FCSTD DOCUMENT  (FreeCAD 0.21R33694 (Git))
Label: archimedes_parametric
License: All rights reserved
LicenseURL: http://en.wikipedia.org/wiki/All_rights_reserved
objects: Part::Part2DObjectPython×3, Part::FeaturePython×3, Sketcher::SketchObject×1, Spreadsheet::Sheet×1
note: 7 computed .brp shape members not serialized (recipe doc carries the construction recipe); baked Part::Feature solids carry a one-line shape summary decoded from their .brp

FEATURE [Sketcher::SketchObject] Sketch
  FullyConstrained = false
  expr: Constraints[51] = <<d>>.diameter
  sketch-geometry (17):
    g0: LineSegment StartX=-33.681 StartY=498.864 StartZ=0 EndX=-186.392 EndY=463.959 EndZ=0
    g1: LineSegment StartX=-209.626 StartY=453.935 StartZ=0 EndX=-339.799 EndY=366.792 EndZ=0
    g2: LineSegment StartX=-347.473 StartY=359.531 StartZ=0 EndX=-441.67 EndY=234.366 EndZ=0
    g3: LineSegment StartX=-462.362 StartY=190.318 StartZ=0 EndX=-498.561 EndY=37.9083 EndZ=0
    g4: LineSegment StartX=-499.91 StartY=-9.4629 StartZ=0 EndX=-472.448 EndY=-163.686 EndZ=0
    g5: LineSegment StartX=-447.113 StartY=-223.808 StartZ=0 EndX=-355.916 EndY=-351.174 EndZ=0
    g6: LineSegment StartX=-314.986 StartY=-388.309 StartZ=0 EndX=-179.372 EndY=-466.718 EndZ=0
    g7: LineSegment StartX=-154.776 StartY=-475.441 StartZ=0 EndX=-0.063336 EndY=-500 EndZ=0
    g8: LineSegment StartX=-22.9551 StartY=-499.473 StartZ=0 EndX=132.724 EndY=-482.063 EndZ=0
    g9: LineSegment StartX=209.626 StartY=-453.935 StartZ=0 EndX=339.799 EndY=-366.792 EndZ=0
    g10: LineSegment StartX=347.473 StartY=-359.531 StartZ=0 EndX=441.67 EndY=-234.366 EndZ=0
    g11: LineSegment StartX=462.362 StartY=-190.318 StartZ=0 EndX=498.561 EndY=-37.9083 EndZ=0
    g12: LineSegment StartX=499.91 StartY=9.4629 StartZ=0 EndX=472.448 EndY=163.686 EndZ=0
    g13: LineSegment StartX=447.113 StartY=223.808 StartZ=0 EndX=355.916 EndY=351.174 EndZ=0
    g14: LineSegment StartX=314.986 StartY=388.309 StartZ=0 EndX=179.372 EndY=466.718 EndZ=0
    g15: Circle CenterX=0 CenterY=0 CenterZ=0 NormalX=0 NormalY=0 NormalZ=1 AngleXU=0 Radius=500
    g16: LineSegment StartX=-1.99667 StartY=499.996 StartZ=0 EndX=152.816 EndY=476.075 EndZ=0
  constraints (42):
    c: Equal(g0, g1-g14) x14
    c: PointOnObject(g0,g15)
    c: PointOnObject(g1,g15)
    c: PointOnObject(g2,g15)
    c: PointOnObject(g3,g15)
    c: PointOnObject(g4,g15)
    c: PointOnObject(g5,g15)
    c: PointOnObject(g6,g15)
    c: PointOnObject(g7,g15)
    c: PointOnObject(g8,g15)
    c: PointOnObject(g9,g15)
    c: PointOnObject(g10,g15)
    c: PointOnObject(g11,g15)
    c: PointOnObject(g12,g15)
    c: PointOnObject(g13,g15)
    c: PointOnObject(g14,g15)
    c: Parallel(g14,g6)
    c: Parallel(g13,g5)
    c: Parallel(g12,g4)
    c: Parallel(g3,g11)
    c: Parallel(g10,g2)
    c: Parallel(g1,g9)
    c: PointOnObject(g14,g15)
    c: PointOnObject(g13,g15)
    c: PointOnObject(g12,g15)
    c: PointOnObject(g11,g15)
    c: PointOnObject(g10,g15)
    c: PointOnObject(g9,g15)
    c: PointOnObject(g8,g15)
    c: PointOnObject(g7,g15)
    c: PointOnObject(g6,g15)
    c: PointOnObject(g5,g15)
    c: PointOnObject(g4,g15)
    c: PointOnObject(g3,g15)
    c: PointOnObject(g2,g15)
    c: PointOnObject(g1,g15)
    c: PointOnObject(g0,g15)
    c: Coincident(g15,g-1)
    c: Diameter(g15) = 1000
    c: PointOnObject(g16,g15)
    c: PointOnObject(g16,g15)
    c: Equal(g16,g14)
FEATURE [Spreadsheet::Sheet] Spreadsheet  label="d"
  cells = A1='diameter; B1(diameter)=1000; C1='mm; A2='thickness; B2(thickness)=5; C2='mm
FEATURE [Part::Part2DObjectPython] Polygon  # Draft 2D object (typed FeaturePython)
  Area = 0
  ChamferSize = 0
  DrawMode = 0
  FacesNumber = 16
  FilletRadius = 0
  MakeFace = false
  Radius = 1000
FEATURE [Part::Part2DObjectPython] Line  # Draft 2D object (typed FeaturePython)
  Area = 0
  ChamferSize = 0
  Closed = false
  End = (0,1000,0)
  FilletRadius = 0
  Length = 1000
  MakeFace = false
  Points = (2) [(0,0,0),(6.12323e-14,1000,0)]
  Start = (0,0,0)
  Subdivisions = 0
FEATURE [Part::FeaturePython] Array  # Draft array (typed FeaturePython)
  Angle = 2
  ArrayType = 1
  Axis = (0,0,1)
  Base = -> Line
  Center = (0,0,0)
  Count = 2
  Fuse = false
  IntervalAxis = (0,0,0)
  IntervalX = (50,0,0)
  IntervalY = (0,50,0)
  IntervalZ = (0,0,50)
  NumberCircles = 3
  NumberPolar = 2
  NumberX = 2
  NumberY = 2
  NumberZ = 1
  RadialDistance = 50
  Symmetry = 1
  TangentialDistance = 25
FEATURE [Part::FeaturePython] Array001  # Draft array (typed FeaturePython)
  Angle = -2
  ArrayType = 1
  Axis = (0,0,1)
  Base = -> Array
  Center = (0,0,0)
  Count = 2
  Fuse = false
  IntervalAxis = (0,0,0)
  IntervalX = (50,0,0)
  IntervalY = (0,50,0)
  IntervalZ = (0,0,50)
  NumberCircles = 3
  NumberPolar = 2
  NumberX = 2
  NumberY = 2
  NumberZ = 1
  RadialDistance = 50
  Symmetry = 1
  TangentialDistance = 25
FEATURE [Part::FeaturePython] Array002  # Draft array (typed FeaturePython)
  Angle = 360
  ArrayType = 1
  Axis = (0,0,1)
  Base = -> Array001
  Center = (0,0,0)
  Count = 16
  Fuse = false
  IntervalAxis = (0,0,0)
  IntervalX = (50,0,0)
  IntervalY = (0,50,0)
  IntervalZ = (0,0,50)
  NumberCircles = 3
  NumberPolar = 16
  NumberX = 2
  NumberY = 2
  NumberZ = 1
  RadialDistance = 50
  Symmetry = 1
  TangentialDistance = 25
FEATURE [Part::Part2DObjectPython] Circle  # Draft 2D object (typed FeaturePython)
  Area = 0
  FirstAngle = 0
  LastAngle = 0
  MakeFace = false
  Radius = 200
